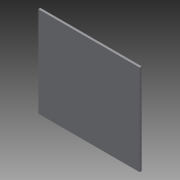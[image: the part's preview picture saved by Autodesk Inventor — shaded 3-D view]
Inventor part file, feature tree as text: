
AUTODESK INVENTOR PART (.ipt)
format: ipt  version: 2014 (Build 180170000, 170)  size: 66,048 bytes
history: native  units: in
note: dims shown in document units (in); Inventor stores cm internally (conversion verified against a paired STEP export)
features: extrude x1, sketch x1
ambient origin geometry x8: Origin, YZ Plane, XZ Plane, XY Plane, X Axis, Y Axis, Z Axis, Center Point
bodies: Solid1 (feature_tree)
feature tree (2):
  extrude  "Extrusion1"  [1 undecoded]
  sketch  "Sketch1"  dims[d0=1.0in d1=0.0in]
note: 1 required parameter value undecoded (feature->parameter linkage not recoverable at this tier; creation-order binding heuristic only, values carry confidence <= 0.55)
